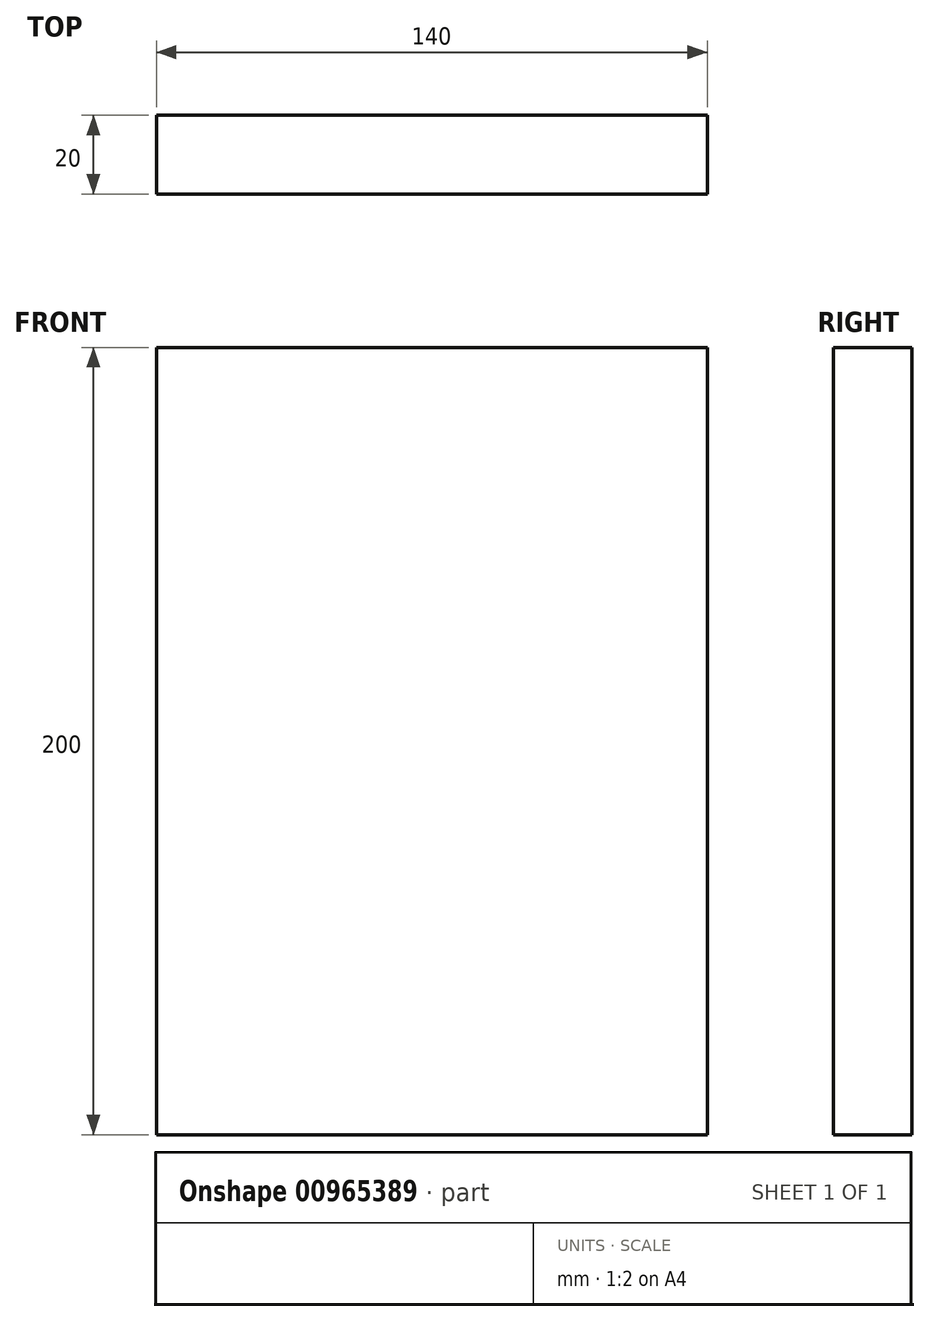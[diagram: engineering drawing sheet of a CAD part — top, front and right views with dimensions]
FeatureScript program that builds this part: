
annotation { "Feature Type Name" : "Feature", "Feature Type Description" : "" }
export const myFeature = defineFeature(function(context is Context, id is Id, definition is map)
    precondition{}
    {
        {
            var Q0;
            Q0=qCreatedBy(makeId("Top.planeOp"),FACE);
            var sketch = newSketch(context, id + "F0", { "sketchPlane" : qUnion([Q0])});
            skLineSegment(sketch, "E0.bottom", {"start": v(70, 10) * mm, "end": v(-70, 10) * mm});
            skLineSegment(sketch, "E0.top", {"start": v(70, -10) * mm, "end": v(-70, -10) * mm});
            skLineSegment(sketch, "E0.left", {"start": v(70, 10) * mm, "end": v(70, -10) * mm});
            skLineSegment(sketch, "E0.right", {"start": v(-70, 10) * mm, "end": v(-70, -10) * mm});
            skPoint(sketch, "E0.middle", {"position": v(0, 0) * mm});
            skSolve(sketch);
        }
        {
            var Q0;
            Q0=makeQuery(id+"F0.imprint","IMPRINT",FACE,{"disambiguationData":[TD([[makeQuery(id+"F0.imprint","IMPRINT",EDGE,{"derivedFrom":sQuery(id+"F0.wireOp",EDGE,"E0.bottom")}),1.0]])]});
            extrude(context, id + "F1", {"entities" : qUnion([Q0]), "depth" : 200 * mm, "offsetDistance" : 25 * mm});
        }
    });
